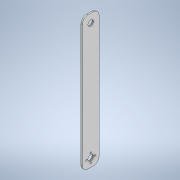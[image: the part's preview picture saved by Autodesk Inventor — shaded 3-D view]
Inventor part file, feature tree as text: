
AUTODESK INVENTOR PART (.ipt)
format: ipt  version: 2020 (Build 240168000, 168)  size: 144,384 bytes
history: native  units: in
note: dims shown in document units (in); Inventor stores cm internally (conversion verified against a paired STEP export)
features: fillet x3, extrude x2, sketch x2
ambient origin geometry x8: Origin, YZ Plane, XZ Plane, XY Plane, X Axis, Y Axis, Z Axis, Center Point
bodies: Solid1 (feature_tree)
feature tree (7):
  extrude  "Extrusion1"  TaperAngle=90.0deg  [1 undecoded]
  extrude  "Extrusion2"  Depth=0.128in TaperAngle=0.0deg
  fillet  "Fillet1"  Radius=0.75in
  fillet  "Fillet2"  Radius=0.5in
  fillet  "Fillet3"  Radius=0.385in
  sketch  "Sketch1"  dims[d0=1.5in d1=90.0deg]
  sketch  "Sketch2"  dims[d2=12.0in d3=0.128in d4=0.0in d5=0.75in d6=0.5in d7=0.385in d8=0.77in d9=0.14in d10=0.14in d11=0.385in d12=0.77in d13=0.14in d14=0.14in d15=1.0in d16=0.0in d17=0.75in d18=0.5in d19=0.5in d20=0.5in d25=0.5in]
note: 1 required parameter value undecoded (feature->parameter linkage not recoverable at this tier; creation-order binding heuristic only, values carry confidence <= 0.55)
